# Revit family: NLRS_57_DUA_UN_round_variable_volume_damper_vvos_LT_Solid_Air
name_source: partatom
category: Duct Accessories
units: mm (PartAtom-declared; Revit-internal decimal feet)

## family parameters
Always vertical = No
Cut with Voids When Loaded = No
Part Type = Breaks Into
Round Connector Dimension = Use Diameter
Shared = No
Work Plane-Based = No

## types (1)
- VVOS
    Assembly Code = 57.70
    Default Elevation = 0 mm  [stored 0 ft]
    Description = Ronde Variabel volume regelaar
    FireRating = 0h
    IfcDescription = Ronde Variabel volume regelaar
    IfcExportAs = IfcDamperType
    IfcExportType = CONTROLDAMPER
    LoadBearing = No
    Manufacturer = Solid Air Climate Solutions
    Model = Variabel volume regelaar - Rond
    NLRS_C_content_datum_uitgifte = 14-04-2023
    NLRS_C_content_provider = Solid Air Climate Systems
    NLRS_C_content_versie = 3.20.01
    NLRS_C_description = Ronde Variabel volume regelaar
    NLRS_C_niveau ontwikkeling = LOD400
    SACS_Cin_Offst = 7 mm  [stored 0.0229659 ft]
    SACS_Cout_Offset = 7 mm  [stored 0.0229659 ft]
    SACS_Data_Hidden = VVOS
    SACS_Dummy = 1
    SACS_Logo_X = 150 mm
    Type Comments = Check flow direction!

note: [stored X ft] marks values corroborated as IEEE doubles in the binary element streams (Revit-internal decimal feet)

## geometry (parser evidence)
native form markers: Sweep x7
no freeform markers — native parametric forms only
